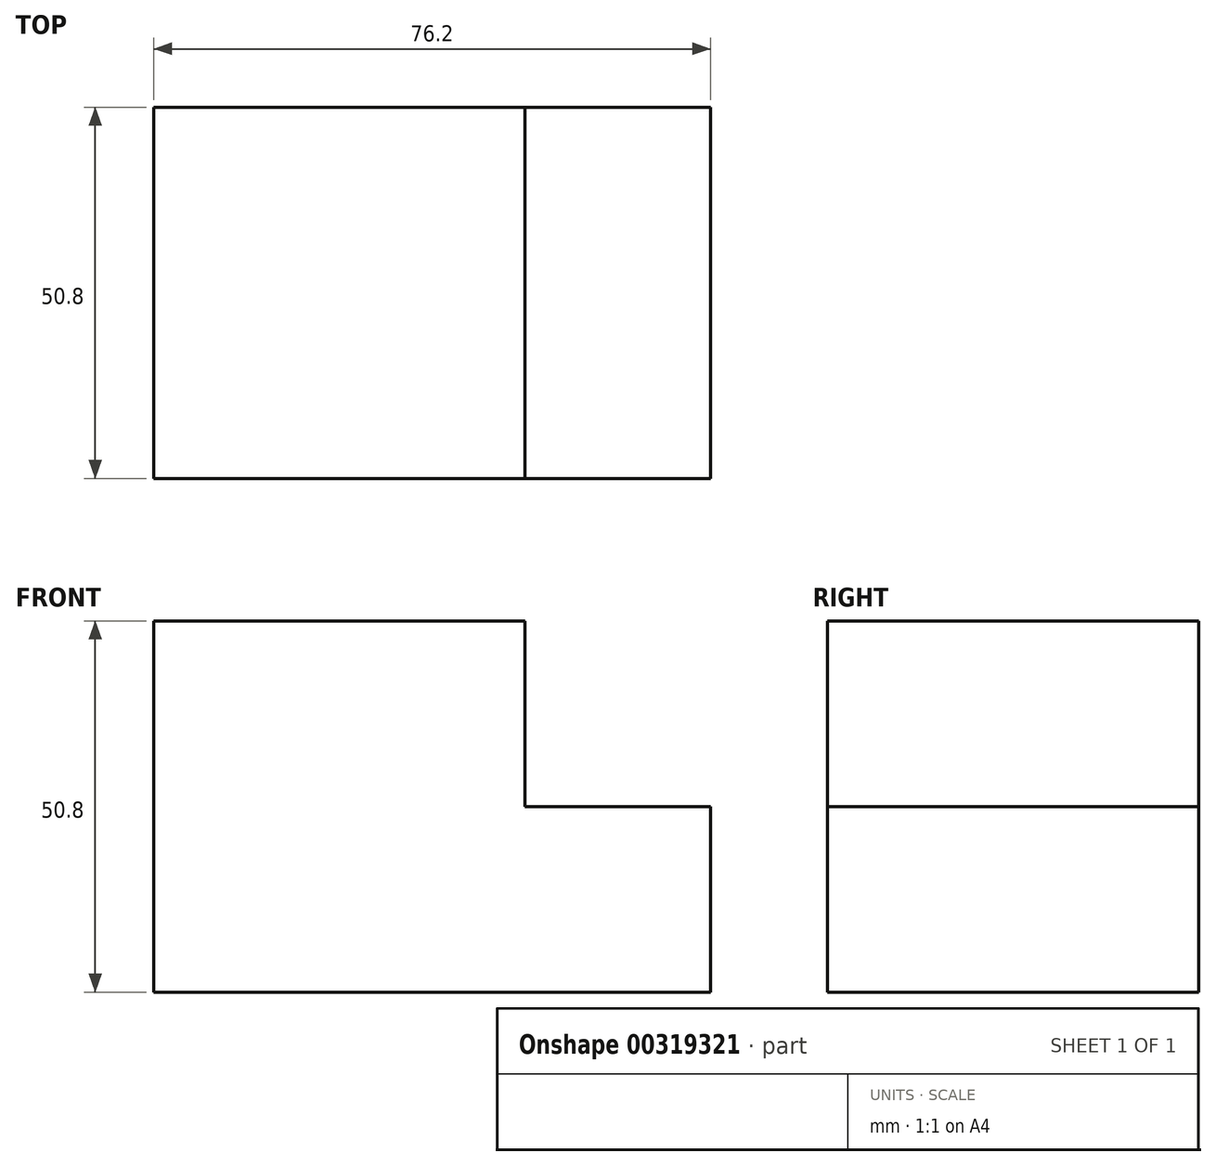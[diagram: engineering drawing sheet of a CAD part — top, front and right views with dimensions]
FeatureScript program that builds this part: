
annotation { "Feature Type Name" : "Feature", "Feature Type Description" : "" }
export const myFeature = defineFeature(function(context is Context, id is Id, definition is map)
    precondition{}
    {
        {
            var Q0;
            Q0=qCreatedBy(makeId("Front.planeOp"),FACE);
            var sketch = newSketch(context, id + "F0", { "sketchPlane" : qUnion([Q0])});
            skLineSegment(sketch, "E0", {"start": v(-40.27, -50.8) * mm, "end": v(35.93, -50.8) * mm});
            skLineSegment(sketch, "E1", {"start": v(35.93, -50.8) * mm, "end": v(35.93, -25.4) * mm});
            skLineSegment(sketch, "E2", {"start": v(35.93, -25.4) * mm, "end": v(10.53, -25.4) * mm});
            skLineSegment(sketch, "E3", {"start": v(10.53, -25.4) * mm, "end": v(10.53, 0) * mm});
            skLineSegment(sketch, "E4", {"start": v(10.53, 0) * mm, "end": v(-40.27, 0) * mm});
            skLineSegment(sketch, "E5", {"start": v(-40.27, 0) * mm, "end": v(-40.27, -50.8) * mm});
            skSolve(sketch);
        }
        {
            var Q0;
            Q0=makeQuery(id+"F0.imprint","IMPRINT",FACE,{"disambiguationData":[TD([[makeQuery(id+"F0.imprint","IMPRINT",EDGE,{"derivedFrom":sQuery(id+"F0.wireOp",EDGE,"E0")}),1.0]])]});
            extrude(context, id + "F1", {"entities" : qUnion([Q0]), "depth" : 50.8 * mm});
        }
    });
